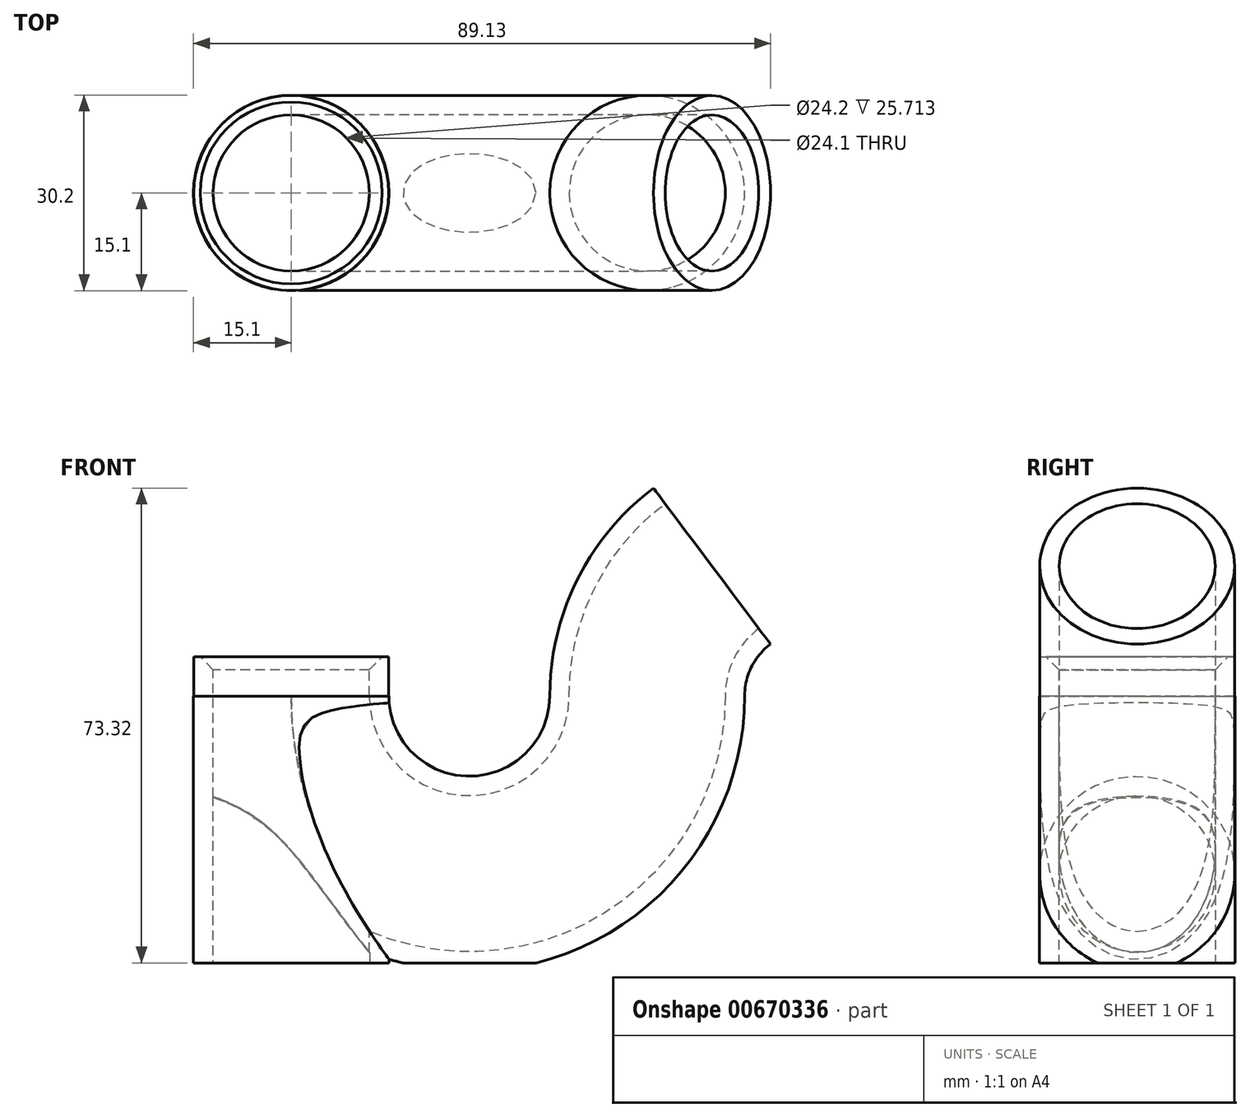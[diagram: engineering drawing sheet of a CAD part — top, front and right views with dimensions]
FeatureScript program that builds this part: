
annotation { "Feature Type Name" : "Feature", "Feature Type Description" : "" }
export const myFeature = defineFeature(function(context is Context, id is Id, definition is map)
    precondition{}
    {
        {
            var Q0;
            Q0=qCreatedBy(makeId("Front.planeOp"),FACE);
            var sketch = newSketch(context, id + "F0", { "sketchPlane" : qUnion([Q0])});
            skArc(sketch, "E0", {"start": v(-65, 0) * mm, "mid": v(-37.5, -27.5) * mm, "end": v(-10, 0) * mm});
            skArc(sketch, "E1", {"start": v(0, 20) * mm, "mid": v(-7.36, 11.18) * mm, "end": v(-10, 0) * mm});
            skLineSegment(sketch, "E2", {"start": v(-10, 0) * mm, "end": v(-10, 25.38) * mm, "construction": true});
            skSolve(sketch);
        }
        {
            var Q0;
            Q0=qCreatedBy(makeId("Top.planeOp"),FACE);
            var sketch = newSketch(context, id + "F1", { "sketchPlane" : qUnion([Q0])});
            skCircle(sketch, "E3", {"center": v(-65, 0) * mm, "radius": 12.05 * mm});
            skCircle(sketch, "E4.0", {"center": v(-65, 0) * mm, "radius": 15.05 * mm});
            skSolve(sketch);
        }
        {
            var Q0;
            Q0=makeQuery(id+"F1.imprint","IMPRINT",FACE,{"disambiguationData":[TD([[makeQuery(id+"F1.imprint","IMPRINT",EDGE,{"derivedFrom":sQuery(id+"F1.wireOp",EDGE,"E3")}),-1.0]])]});
            var Q1;
            Q1=sQuery(id+"F0.wireOp",EDGE,"E0");
            var Q2;
            Q2=sQuery(id+"F0.wireOp",EDGE,"E1");
            sweep(context, id + "F2", {"profiles" : qUnion([Q0]), "path" : qUnion([Q1, Q2])});
        }
        {
            var Q0;
            Q0=makeQuery(id+"F2.opSweep","CAP_FACE",FACE,{"disambiguationData":[OSD([sQuery(id+"F0.wireOp",VERTEX,"E1.start"),sQuery(id+"F1.wireOp",EDGE,"E3"),sQuery(id+"F1.wireOp",EDGE,"E4.0")])],"isStart":false});
            var sketch = newSketch(context, id + "F3", { "sketchPlane" : qUnion([Q0])});
            skLineSegment(sketch, "E5", {"start": v(0, 0) * mm, "end": v(0, 16) * mm, "construction": true});
            skLineSegment(sketch, "E6", {"start": v(0, 16) * mm, "end": v(-15.05, 16) * mm});
            skLineSegment(sketch, "E7", {"start": v(0, 16) * mm, "end": v(15.05, 16) * mm});
            skArc(sketch, "E8", {"start": v(-15.05, 16) * mm, "mid": v(0, 0.95) * mm, "end": v(15.05, 16) * mm});
            skSolve(sketch);
        }
        {
            var Q0;
            Q0=makeQuery(id+"F1.imprint","IMPRINT",FACE,{"disambiguationData":[TD([[makeQuery(id+"F1.imprint","IMPRINT",EDGE,{"derivedFrom":sQuery(id+"F1.wireOp",EDGE,"E3")}),1.0]])]});
            extrude(context, id + "F4", {"entities" : qUnion([Q0]), "operationType" : NewBodyOperationType.REMOVE, "endBound" : BoundingType.THROUGH_ALL, "oppositeDirection" : true, "depth" : 25 * mm, "offsetDistance" : 25 * mm});
        }
        {
            var Q0;
            Q0=makeQuery(id+"F1.imprint","IMPRINT",FACE,{"disambiguationData":[TD([[makeQuery(id+"F1.imprint","IMPRINT",EDGE,{"derivedFrom":sQuery(id+"F1.wireOp",EDGE,"E3")}),-1.0]])]});
            extrude(context, id + "F5", {"entities" : qUnion([Q0]), "operationType" : NewBodyOperationType.ADD, "depth" : 6 * mm, "offsetDistance" : 25 * mm});
        }
        {
            var Q0;
            Q0=qCreatedBy(makeId("Top.planeOp"),FACE);
            cPlane(context, id + "F6", {"entities" : qUnion([Q0]), "cplaneType" : CPlaneType.OFFSET, "offset" : 46.9 * mm, "oppositeDirection" : true, "width" : 150 * mm, "height" : 150 * mm});
        }
        {
            var Q0;
            Q0=qCreatedBy(id+"F6.planeOp",FACE);
            var sketch = newSketch(context, id + "F7", { "sketchPlane" : qUnion([Q0])});
            skCircle(sketch, "E9", {"center": v(-65, 0) * mm, "radius": 12.1 * mm});
            skCircle(sketch, "E10.0", {"center": v(-65, 0) * mm, "radius": 15.1 * mm});
            skSolve(sketch);
        }
        {
            var Q0;
            Q0=makeQuery(id+"F7.imprint","IMPRINT",FACE,{"disambiguationData":[TD([[makeQuery(id+"F7.imprint","IMPRINT",EDGE,{"derivedFrom":sQuery(id+"F7.wireOp",EDGE,"E9")}),-1.0]])]});
            extrude(context, id + "F8", {"entities" : qUnion([Q0]), "operationType" : NewBodyOperationType.ADD, "depth" : 46.8 * mm, "offsetDistance" : 25 * mm});
        }
        {
            var Q0;
            Q0=makeQuery(id+"F1.imprint","IMPRINT",FACE,{"disambiguationData":[TD([[makeQuery(id+"F1.imprint","IMPRINT",EDGE,{"derivedFrom":sQuery(id+"F1.wireOp",EDGE,"E3")}),1.0]])]});
            var Q1;
            Q1=sQuery(id+"F0.wireOp",EDGE,"E0");
            sweep(context, id + "F9", {"operationType" : NewBodyOperationType.REMOVE, "profiles" : qUnion([Q0]), "path" : qUnion([Q1])});
        }
        {
            var Q0;
            Q0=qCreatedBy(makeId("Front.planeOp"),FACE);
            var sketch = newSketch(context, id + "F10", { "sketchPlane" : qUnion([Q0])});
            skLineSegment(sketch, "E11.bottom", {"start": v(-140.36, -66.32) * mm, "end": v(99.15, -66.32) * mm});
            skLineSegment(sketch, "E11.top", {"start": v(-140.36, -41.28) * mm, "end": v(99.15, -41.28) * mm});
            skLineSegment(sketch, "E11.left", {"start": v(-140.36, -66.32) * mm, "end": v(-140.36, -41.28) * mm});
            skLineSegment(sketch, "E11.right", {"start": v(99.15, -66.32) * mm, "end": v(99.15, -41.28) * mm});
            skSolve(sketch);
        }
        {
            var Q0;
            Q0=makeQuery(id+"F10.imprint","IMPRINT",FACE,{"disambiguationData":[TD([[makeQuery(id+"F10.imprint","IMPRINT",EDGE,{"derivedFrom":sQuery(id+"F10.wireOp",EDGE,"E11.bottom")}),1.0]])]});
            extrude(context, id + "F11", {"entities" : qUnion([Q0]), "operationType" : NewBodyOperationType.REMOVE, "endBound" : BoundingType.SYMMETRIC, "oppositeDirection" : true, "depth" : 50 * mm, "offsetDistance" : 25 * mm});
        }
        {
            var Q0;
            Q0=makeQuery(id+"F5.opExtrude","CAP_EDGE",EDGE,{"disambiguationData":[OSD([sQuery(id+"F1.wireOp",EDGE,"E3")])],"isStart":false});
            chamfer(context, id + "F12", {"entities" : qUnion([Q0]), "width" : 2 * mm, "tangentPropagation" : true});
        }
    });
